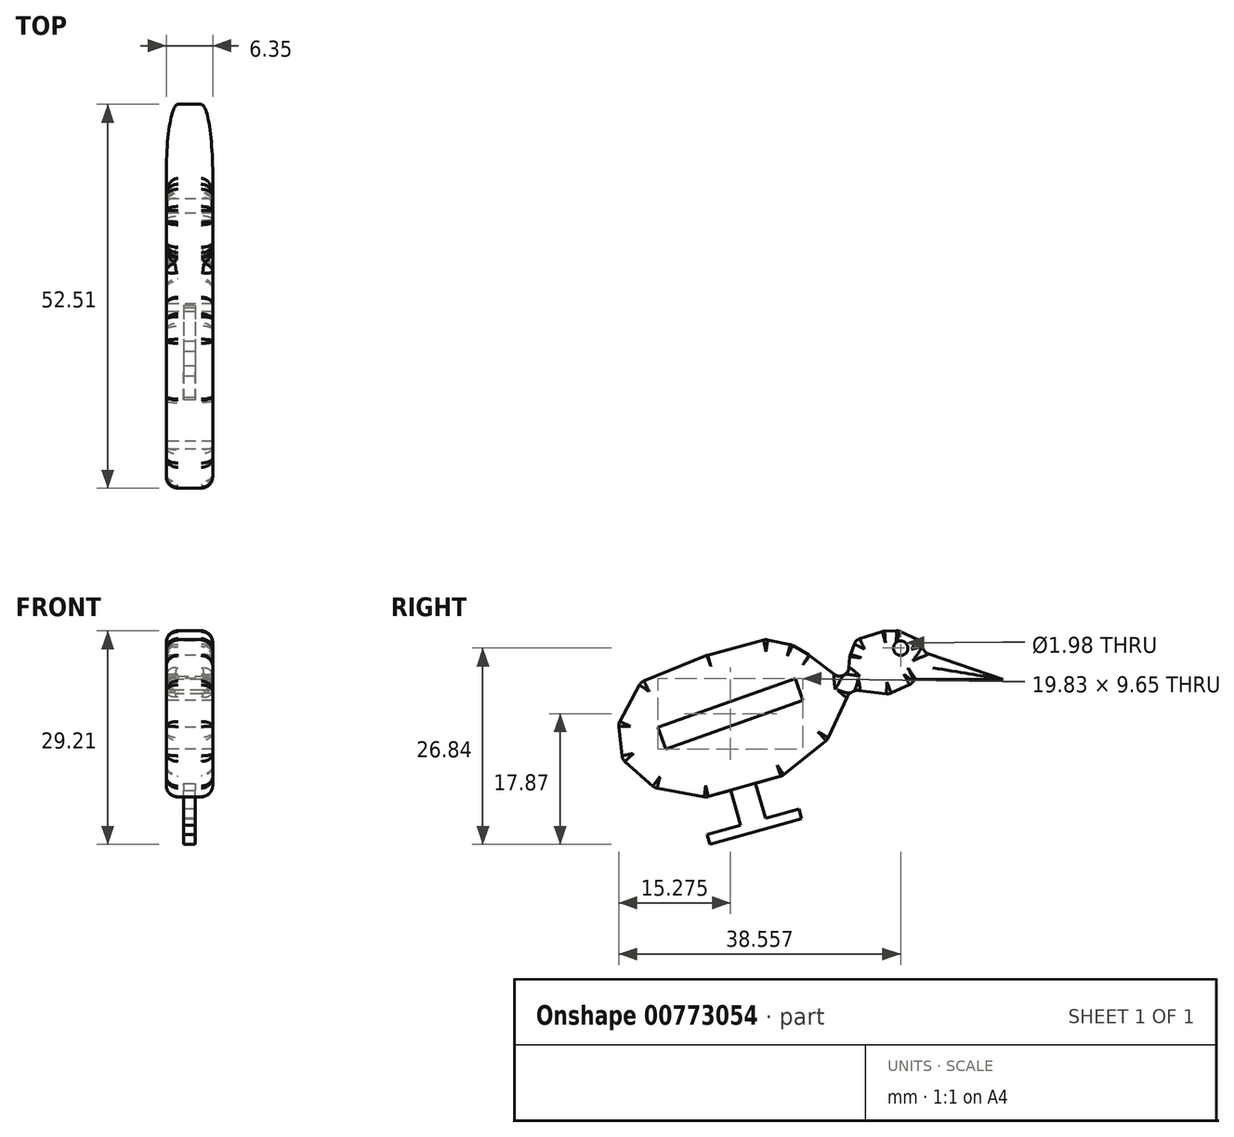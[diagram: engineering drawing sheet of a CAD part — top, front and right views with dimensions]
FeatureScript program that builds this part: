
annotation { "Feature Type Name" : "Feature", "Feature Type Description" : "" }
export const myFeature = defineFeature(function(context is Context, id is Id, definition is map)
    precondition{}
    {
        {
            var Q0;
            Q0=qCreatedBy(makeId("Right.planeOp"),FACE);
            var sketch = newSketch(context, id + "F0", { "sketchPlane" : qUnion([Q0])});
            skLineSegment(sketch, "E0", {"start": v(145.45, 30.35) * mm, "end": v(93.93, 53.96) * mm});
            skLineSegment(sketch, "E1", {"start": v(93.93, 53.96) * mm, "end": v(60.65, 52.9) * mm});
            skLineSegment(sketch, "E2", {"start": v(60.65, 52.9) * mm, "end": v(0, 33.57) * mm});
            skLineSegment(sketch, "E3", {"start": v(-15.57, -37.47) * mm, "end": v(-36.88, -49.23) * mm});
            skLineSegment(sketch, "E4", {"start": v(-469.64, -58.75) * mm, "end": v(-324.72, 0) * mm});
            skLineSegment(sketch, "E5", {"start": v(-469.64, -58.75) * mm, "end": v(-519.02, -150) * mm});
            skLineSegment(sketch, "E6", {"start": v(-519.02, -150) * mm, "end": v(-510.43, -227.28) * mm});
            skLineSegment(sketch, "E7", {"start": v(-510.43, -227.28) * mm, "end": v(-439.58, -289.54) * mm});
            skLineSegment(sketch, "E8", {"start": v(-439.58, -289.54) * mm, "end": v(-326.86, -310.3) * mm});
            skLineSegment(sketch, "E9", {"start": v(-326.86, -310.3) * mm, "end": v(-159.98, -263.53) * mm});
            skLineSegment(sketch, "E10", {"start": v(-159.98, -263.53) * mm, "end": v(-61.37, -183.89) * mm});
            skLineSegment(sketch, "E11", {"start": v(-61.37, -183.89) * mm, "end": v(-15.57, -84.51) * mm});
            skLineSegment(sketch, "E12", {"start": v(-15.57, -84.51) * mm, "end": v(0, -75.92) * mm});
            skLineSegment(sketch, "E13", {"start": v(122.91, -61.97) * mm, "end": v(72.46, -84.51) * mm});
            skLineSegment(sketch, "E14", {"start": v(72.46, -84.51) * mm, "end": v(0, -75.92) * mm});
            skLineSegment(sketch, "E15", {"start": v(122.91, -61.97) * mm, "end": v(150.82, -16.88) * mm});
            skLineSegment(sketch, "E16", {"start": v(150.82, -16.88) * mm, "end": v(145.45, 30.35) * mm});
            skLineSegment(sketch, "E17", {"start": v(0, 33.57) * mm, "end": v(-12.35, 0) * mm});
            skLineSegment(sketch, "E18", {"start": v(-12.35, 0) * mm, "end": v(-15.57, -37.47) * mm});
            skLineSegment(sketch, "E19", {"start": v(-36.88, -49.23) * mm, "end": v(-101.34, 0) * mm});
            skLineSegment(sketch, "E20", {"start": v(-101.34, 0) * mm, "end": v(-140.09, 22.83) * mm});
            skLineSegment(sketch, "E21", {"start": v(-140.09, 22.83) * mm, "end": v(-196.98, 34.64) * mm});
            skLineSegment(sketch, "E22", {"start": v(-196.98, 34.64) * mm, "end": v(-324.72, 0) * mm});
            skLineSegment(sketch, "E23", {"start": v(148.14, 6.73) * mm, "end": v(321.78, -52.74) * mm});
            skLineSegment(sketch, "E24", {"start": v(321.78, -52.74) * mm, "end": v(128.63, -52.74) * mm});
            skSolve(sketch);
        }
        {
            var Q0;
            {var subQ4=sQuery(id+"F0.wireOp",EDGE,"E23");Q0=makeQuery(id+"F0.imprint","IMPRINT",FACE,{"disambiguationData":[TD([[makeQuery(id+"F0.imprint","IMPRINT",EDGE,{"derivedFrom":subQ4}),-1.0]])]});}
            var Q1;
            {var subQ1=sQuery(id+"F0.wireOp",EDGE,"E0");Q1=makeQuery(id+"F0.imprint","IMPRINT",FACE,{"disambiguationData":[TD([[makeQuery(id+"F0.imprint","IMPRINT",EDGE,{"derivedFrom":subQ1}),1.0]])]});}
            extrude(context, id + "F1", {"entities" : qUnion([Q0, Q1]), "depth" : 101.6 * mm, "offsetDistance" : 25.4 * mm});
        }
        {
            var Q0;
            Q0=makeQuery(id+"F1.opExtrude","CAP_EDGE",EDGE,{"disambiguationData":[OSD([sQuery(id+"F0.wireOp",EDGE,"E18")])],"isStart":false});
            var Q1;
            Q1=makeQuery(id+"F1.opExtrude","CAP_EDGE",EDGE,{"disambiguationData":[OSD([sQuery(id+"F0.wireOp",EDGE,"E17")])],"isStart":false});
            var Q2;
            Q2=makeQuery(id+"F1.opExtrude","CAP_EDGE",EDGE,{"disambiguationData":[OSD([sQuery(id+"F0.wireOp",EDGE,"E2")])],"isStart":false});
            var Q3;
            Q3=makeQuery(id+"F1.opExtrude","CAP_EDGE",EDGE,{"disambiguationData":[OSD([sQuery(id+"F0.wireOp",EDGE,"E1")])],"isStart":false});
            var Q4;
            Q4=makeQuery(id+"F1.opExtrude","CAP_EDGE",EDGE,{"disambiguationData":[OSD([sQuery(id+"F0.wireOp",EDGE,"E0")])],"isStart":false});
            var Q5;
            Q5=makeQuery(id+"F1.opExtrude","CAP_EDGE",EDGE,{"disambiguationData":[OSD([sQuery(id+"F0.wireOp",EDGE,"E16")])],"isStart":false});
            var Q6;
            Q6=makeQuery(id+"F1.opExtrude","CAP_EDGE",EDGE,{"disambiguationData":[OSD([sQuery(id+"F0.wireOp",EDGE,"E23")])],"isStart":false});
            var Q7;
            Q7=makeQuery(id+"F1.opExtrude","CAP_EDGE",EDGE,{"disambiguationData":[OSD([sQuery(id+"F0.wireOp",EDGE,"E14")])],"isStart":false});
            var Q8;
            Q8=makeQuery(id+"F1.opExtrude","CAP_EDGE",EDGE,{"disambiguationData":[OSD([sQuery(id+"F0.wireOp",EDGE,"E13")])],"isStart":false});
            var Q9;
            Q9=makeQuery(id+"F1.opExtrude","CAP_EDGE",EDGE,{"disambiguationData":[OSD([sQuery(id+"F0.wireOp",EDGE,"E15")])],"isStart":false});
            var Q10;
            Q10=makeQuery(id+"F1.opExtrude","CAP_EDGE",EDGE,{"disambiguationData":[OSD([sQuery(id+"F0.wireOp",EDGE,"E24")])],"isStart":false});
            fillet(context, id + "F2", {"entities" : qUnion([Q0, Q1, Q2, Q3, Q4, Q5, Q6, Q7, Q8, Q9, Q10]), "radius" : 25.4 * mm, "tangentPropagation" : true, "allowEdgeOverflow" : false});
        }
        {
            var Q0;
            Q0=makeQuery(id+"F1.opExtrude","CAP_EDGE",EDGE,{"disambiguationData":[OSD([sQuery(id+"F0.wireOp",EDGE,"E23")])],"isStart":true});
            var Q1;
            Q1=makeQuery(id+"F1.opExtrude","CAP_EDGE",EDGE,{"disambiguationData":[OSD([sQuery(id+"F0.wireOp",EDGE,"E16")])],"isStart":true});
            var Q2;
            Q2=makeQuery(id+"F1.opExtrude","CAP_EDGE",EDGE,{"disambiguationData":[OSD([sQuery(id+"F0.wireOp",EDGE,"E1")])],"isStart":true});
            var Q3;
            Q3=makeQuery(id+"F1.opExtrude","CAP_EDGE",EDGE,{"disambiguationData":[OSD([sQuery(id+"F0.wireOp",EDGE,"E0")])],"isStart":true});
            var Q4;
            Q4=makeQuery(id+"F1.opExtrude","CAP_EDGE",EDGE,{"disambiguationData":[OSD([sQuery(id+"F0.wireOp",EDGE,"E2")])],"isStart":true});
            var Q5;
            Q5=makeQuery(id+"F1.opExtrude","CAP_EDGE",EDGE,{"disambiguationData":[OSD([sQuery(id+"F0.wireOp",EDGE,"E17")])],"isStart":true});
            var Q6;
            Q6=makeQuery(id+"F1.opExtrude","CAP_EDGE",EDGE,{"disambiguationData":[OSD([sQuery(id+"F0.wireOp",EDGE,"E18")])],"isStart":true});
            var Q7;
            Q7=makeQuery(id+"F1.opExtrude","CAP_EDGE",EDGE,{"disambiguationData":[OSD([sQuery(id+"F0.wireOp",EDGE,"E14")])],"isStart":true});
            var Q8;
            Q8=makeQuery(id+"F1.opExtrude","CAP_EDGE",EDGE,{"disambiguationData":[OSD([sQuery(id+"F0.wireOp",EDGE,"E13")])],"isStart":true});
            var Q9;
            Q9=makeQuery(id+"F1.opExtrude","CAP_EDGE",EDGE,{"disambiguationData":[OSD([sQuery(id+"F0.wireOp",EDGE,"E15")])],"isStart":true});
            var Q10;
            Q10=makeQuery(id+"F1.opExtrude","CAP_EDGE",EDGE,{"disambiguationData":[OSD([sQuery(id+"F0.wireOp",EDGE,"E24")])],"isStart":true});
            fillet(context, id + "F3", {"entities" : qUnion([Q0, Q1, Q2, Q3, Q4, Q5, Q6, Q7, Q8, Q9, Q10]), "radius" : 25.4 * mm, "tangentPropagation" : true, "allowEdgeOverflow" : false});
        }
        {
            var Q0;
            Q0=makeQuery(id+"F1.opExtrude","CAP_EDGE",EDGE,{"disambiguationData":[OSD([sQuery(id+"F0.wireOp",EDGE,"E3")])],"isStart":true});
            var Q1;
            Q1=makeQuery(id+"F1.opExtrude","CAP_EDGE",EDGE,{"disambiguationData":[OSD([sQuery(id+"F0.wireOp",EDGE,"E12")])],"isStart":true});
            var Q2;
            Q2=makeQuery(id+"F1.opExtrude","CAP_EDGE",EDGE,{"disambiguationData":[OSD([sQuery(id+"F0.wireOp",EDGE,"E3")])],"isStart":false});
            var Q3;
            Q3=makeQuery(id+"F1.opExtrude","CAP_EDGE",EDGE,{"disambiguationData":[OSD([sQuery(id+"F0.wireOp",EDGE,"E12")])],"isStart":false});
            fillet(context, id + "F4", {"entities" : qUnion([Q0, Q1, Q2, Q3]), "radius" : 19.05 * mm, "tangentPropagation" : true, "allowEdgeOverflow" : false});
        }
        {
            var Q0;
            Q0=makeQuery(id+"F1.opExtrude","CAP_EDGE",EDGE,{"disambiguationData":[OSD([sQuery(id+"F0.wireOp",EDGE,"E19")])],"isStart":true});
            var Q1;
            Q1=makeQuery(id+"F1.opExtrude","CAP_EDGE",EDGE,{"disambiguationData":[OSD([sQuery(id+"F0.wireOp",EDGE,"E11")])],"isStart":true});
            var Q2;
            Q2=makeQuery(id+"F1.opExtrude","CAP_EDGE",EDGE,{"disambiguationData":[OSD([sQuery(id+"F0.wireOp",EDGE,"E10")])],"isStart":true});
            var Q3;
            Q3=makeQuery(id+"F1.opExtrude","CAP_EDGE",EDGE,{"disambiguationData":[OSD([sQuery(id+"F0.wireOp",EDGE,"E9")])],"isStart":true});
            var Q4;
            Q4=makeQuery(id+"F1.opExtrude","CAP_EDGE",EDGE,{"disambiguationData":[OSD([sQuery(id+"F0.wireOp",EDGE,"E8")])],"isStart":true});
            var Q5;
            Q5=makeQuery(id+"F1.opExtrude","CAP_EDGE",EDGE,{"disambiguationData":[OSD([sQuery(id+"F0.wireOp",EDGE,"E7")])],"isStart":true});
            var Q6;
            Q6=makeQuery(id+"F1.opExtrude","CAP_EDGE",EDGE,{"disambiguationData":[OSD([sQuery(id+"F0.wireOp",EDGE,"E6")])],"isStart":true});
            var Q7;
            Q7=makeQuery(id+"F1.opExtrude","CAP_EDGE",EDGE,{"disambiguationData":[OSD([sQuery(id+"F0.wireOp",EDGE,"E5")])],"isStart":true});
            var Q8;
            Q8=makeQuery(id+"F1.opExtrude","CAP_EDGE",EDGE,{"disambiguationData":[OSD([sQuery(id+"F0.wireOp",EDGE,"E4")])],"isStart":true});
            var Q9;
            Q9=makeQuery(id+"F1.opExtrude","CAP_EDGE",EDGE,{"disambiguationData":[OSD([sQuery(id+"F0.wireOp",EDGE,"E22")])],"isStart":true});
            var Q10;
            Q10=makeQuery(id+"F1.opExtrude","CAP_EDGE",EDGE,{"disambiguationData":[OSD([sQuery(id+"F0.wireOp",EDGE,"E21")])],"isStart":true});
            var Q11;
            Q11=makeQuery(id+"F1.opExtrude","CAP_EDGE",EDGE,{"disambiguationData":[OSD([sQuery(id+"F0.wireOp",EDGE,"E20")])],"isStart":true});
            var Q12;
            Q12=makeQuery(id+"F1.opExtrude","CAP_EDGE",EDGE,{"disambiguationData":[OSD([sQuery(id+"F0.wireOp",EDGE,"E6")])],"isStart":false});
            var Q13;
            Q13=makeQuery(id+"F1.opExtrude","CAP_EDGE",EDGE,{"disambiguationData":[OSD([sQuery(id+"F0.wireOp",EDGE,"E5")])],"isStart":false});
            var Q14;
            Q14=makeQuery(id+"F1.opExtrude","CAP_EDGE",EDGE,{"disambiguationData":[OSD([sQuery(id+"F0.wireOp",EDGE,"E7")])],"isStart":false});
            var Q15;
            Q15=makeQuery(id+"F1.opExtrude","CAP_EDGE",EDGE,{"disambiguationData":[OSD([sQuery(id+"F0.wireOp",EDGE,"E8")])],"isStart":false});
            var Q16;
            Q16=makeQuery(id+"F1.opExtrude","CAP_EDGE",EDGE,{"disambiguationData":[OSD([sQuery(id+"F0.wireOp",EDGE,"E9")])],"isStart":false});
            var Q17;
            Q17=makeQuery(id+"F1.opExtrude","CAP_EDGE",EDGE,{"disambiguationData":[OSD([sQuery(id+"F0.wireOp",EDGE,"E10")])],"isStart":false});
            var Q18;
            Q18=makeQuery(id+"F1.opExtrude","CAP_EDGE",EDGE,{"disambiguationData":[OSD([sQuery(id+"F0.wireOp",EDGE,"E11")])],"isStart":false});
            var Q19;
            Q19=makeQuery(id+"F1.opExtrude","CAP_EDGE",EDGE,{"disambiguationData":[OSD([sQuery(id+"F0.wireOp",EDGE,"E19")])],"isStart":false});
            var Q20;
            Q20=makeQuery(id+"F1.opExtrude","CAP_EDGE",EDGE,{"disambiguationData":[OSD([sQuery(id+"F0.wireOp",EDGE,"E20")])],"isStart":false});
            var Q21;
            Q21=makeQuery(id+"F1.opExtrude","CAP_EDGE",EDGE,{"disambiguationData":[OSD([sQuery(id+"F0.wireOp",EDGE,"E21")])],"isStart":false});
            var Q22;
            Q22=makeQuery(id+"F1.opExtrude","CAP_EDGE",EDGE,{"disambiguationData":[OSD([sQuery(id+"F0.wireOp",EDGE,"E4")])],"isStart":false});
            var Q23;
            Q23=makeQuery(id+"F1.opExtrude","CAP_EDGE",EDGE,{"disambiguationData":[OSD([sQuery(id+"F0.wireOp",EDGE,"E22")])],"isStart":false});
            fillet(context, id + "F5", {"entities" : qUnion([Q0, Q1, Q2, Q3, Q4, Q5, Q6, Q7, Q8, Q9, Q10, Q11, Q12, Q13, Q14, Q15, Q16, Q17, Q18, Q19, Q20, Q21, Q22, Q23]), "radius" : 25.4 * mm, "tangentPropagation" : true, "allowEdgeOverflow" : false});
        }
        {
            var Q0;
            Q0=makeQuery(id+"F1.opExtrude","SWEPT_EDGE",EDGE,{"disambiguationData":[OSD([sQuery(id+"F0.wireOp",EDGE,"E15"),sQuery(id+"F0.wireOp",EDGE,"E24")])]});
            fillet(context, id + "F6", {"entities" : qUnion([Q0]), "radius" : 5.08 * mm, "tangentPropagation" : true, "allowEdgeOverflow" : false});
        }
        {
            var Q0;
            Q0=makeQuery(id+"F1.opExtrude","SWEPT_EDGE",EDGE,{"disambiguationData":[OSD([sQuery(id+"F0.wireOp",EDGE,"E13"),sQuery(id+"F0.wireOp",EDGE,"E15")])]});
            var Q1;
            Q1=makeQuery(id+"F1.opExtrude","SWEPT_EDGE",EDGE,{"disambiguationData":[OSD([sQuery(id+"F0.wireOp",EDGE,"E13"),sQuery(id+"F0.wireOp",EDGE,"E14")])]});
            var Q2;
            Q2=makeQuery(id+"F1.opExtrude","SWEPT_EDGE",EDGE,{"disambiguationData":[OSD([sQuery(id+"F0.wireOp",EDGE,"E12"),sQuery(id+"F0.wireOp",EDGE,"E14")])]});
            var Q3;
            Q3=makeQuery(id+"F1.opExtrude","SWEPT_EDGE",EDGE,{"disambiguationData":[OSD([sQuery(id+"F0.wireOp",EDGE,"E11"),sQuery(id+"F0.wireOp",EDGE,"E12")])]});
            var Q4;
            Q4=makeQuery(id+"F1.opExtrude","SWEPT_EDGE",EDGE,{"disambiguationData":[OSD([sQuery(id+"F0.wireOp",EDGE,"E10"),sQuery(id+"F0.wireOp",EDGE,"E11")])]});
            var Q5;
            Q5=makeQuery(id+"F1.opExtrude","SWEPT_EDGE",EDGE,{"disambiguationData":[OSD([sQuery(id+"F0.wireOp",EDGE,"E9"),sQuery(id+"F0.wireOp",EDGE,"E10")])]});
            var Q6;
            Q6=makeQuery(id+"F1.opExtrude","SWEPT_EDGE",EDGE,{"disambiguationData":[OSD([sQuery(id+"F0.wireOp",EDGE,"E8"),sQuery(id+"F0.wireOp",EDGE,"E9")])]});
            var Q7;
            Q7=makeQuery(id+"F1.opExtrude","SWEPT_EDGE",EDGE,{"disambiguationData":[OSD([sQuery(id+"F0.wireOp",EDGE,"E7"),sQuery(id+"F0.wireOp",EDGE,"E8")])]});
            var Q8;
            Q8=makeQuery(id+"F1.opExtrude","SWEPT_EDGE",EDGE,{"disambiguationData":[OSD([sQuery(id+"F0.wireOp",EDGE,"E6"),sQuery(id+"F0.wireOp",EDGE,"E7")])]});
            var Q9;
            Q9=makeQuery(id+"F1.opExtrude","SWEPT_EDGE",EDGE,{"disambiguationData":[OSD([sQuery(id+"F0.wireOp",EDGE,"E5"),sQuery(id+"F0.wireOp",EDGE,"E6")])]});
            var Q10;
            Q10=makeQuery(id+"F1.opExtrude","SWEPT_EDGE",EDGE,{"disambiguationData":[OSD([sQuery(id+"F0.wireOp",EDGE,"E4"),sQuery(id+"F0.wireOp",EDGE,"E5")])]});
            var Q11;
            Q11=makeQuery(id+"F1.opExtrude","SWEPT_EDGE",EDGE,{"disambiguationData":[OSD([sQuery(id+"F0.wireOp",EDGE,"E4"),sQuery(id+"F0.wireOp",EDGE,"E22")])]});
            var Q12;
            Q12=makeQuery(id+"F1.opExtrude","SWEPT_EDGE",EDGE,{"disambiguationData":[OSD([sQuery(id+"F0.wireOp",EDGE,"E21"),sQuery(id+"F0.wireOp",EDGE,"E22")])]});
            var Q13;
            Q13=makeQuery(id+"F1.opExtrude","SWEPT_EDGE",EDGE,{"disambiguationData":[OSD([sQuery(id+"F0.wireOp",EDGE,"E20"),sQuery(id+"F0.wireOp",EDGE,"E21")])]});
            var Q14;
            Q14=makeQuery(id+"F1.opExtrude","SWEPT_EDGE",EDGE,{"disambiguationData":[OSD([sQuery(id+"F0.wireOp",EDGE,"E19"),sQuery(id+"F0.wireOp",EDGE,"E20")])]});
            var Q15;
            Q15=makeQuery(id+"F1.opExtrude","SWEPT_EDGE",EDGE,{"disambiguationData":[OSD([sQuery(id+"F0.wireOp",EDGE,"E3"),sQuery(id+"F0.wireOp",EDGE,"E19")])]});
            var Q16;
            Q16=makeQuery(id+"F1.opExtrude","SWEPT_EDGE",EDGE,{"disambiguationData":[OSD([sQuery(id+"F0.wireOp",EDGE,"E3"),sQuery(id+"F0.wireOp",EDGE,"E18")])]});
            var Q17;
            Q17=makeQuery(id+"F1.opExtrude","SWEPT_EDGE",EDGE,{"disambiguationData":[OSD([sQuery(id+"F0.wireOp",EDGE,"E17"),sQuery(id+"F0.wireOp",EDGE,"E18")])]});
            var Q18;
            Q18=makeQuery(id+"F1.opExtrude","SWEPT_EDGE",EDGE,{"disambiguationData":[OSD([sQuery(id+"F0.wireOp",EDGE,"E2"),sQuery(id+"F0.wireOp",EDGE,"E17")])]});
            var Q19;
            Q19=makeQuery(id+"F1.opExtrude","SWEPT_EDGE",EDGE,{"disambiguationData":[OSD([sQuery(id+"F0.wireOp",EDGE,"E1"),sQuery(id+"F0.wireOp",EDGE,"E2")])]});
            var Q20;
            Q20=makeQuery(id+"F1.opExtrude","SWEPT_EDGE",EDGE,{"disambiguationData":[OSD([sQuery(id+"F0.wireOp",EDGE,"E0"),sQuery(id+"F0.wireOp",EDGE,"E1")])]});
            var Q21;
            Q21=makeQuery(id+"F1.opExtrude","SWEPT_EDGE",EDGE,{"disambiguationData":[OSD([sQuery(id+"F0.wireOp",EDGE,"E0"),sQuery(id+"F0.wireOp",EDGE,"E16")])]});
            var Q22;
            Q22=makeQuery(id+"F1.opExtrude","SWEPT_EDGE",EDGE,{"disambiguationData":[OSD([sQuery(id+"F0.wireOp",EDGE,"E16"),sQuery(id+"F0.wireOp",EDGE,"E23")])]});
            fillet(context, id + "F7", {"entities" : qUnion([Q0, Q1, Q2, Q3, Q4, Q5, Q6, Q7, Q8, Q9, Q10, Q11, Q12, Q13, Q14, Q15, Q16, Q17, Q18, Q19, Q20, Q21, Q22]), "radius" : 19.05 * mm, "tangentPropagation" : true, "allowEdgeOverflow" : false});
        }
        {
            var Q0;
            Q0=makeQuery(id+"F1.opExtrude","CAP_FACE",FACE,{"disambiguationData":[OSD([sQuery(id+"F0.wireOp",EDGE,"E0"),sQuery(id+"F0.wireOp",EDGE,"E1"),sQuery(id+"F0.wireOp",EDGE,"E2"),sQuery(id+"F0.wireOp",EDGE,"E3"),sQuery(id+"F0.wireOp",EDGE,"E4"),sQuery(id+"F0.wireOp",EDGE,"E5"),sQuery(id+"F0.wireOp",EDGE,"E6"),sQuery(id+"F0.wireOp",EDGE,"E7"),sQuery(id+"F0.wireOp",EDGE,"E8"),sQuery(id+"F0.wireOp",EDGE,"E9"),sQuery(id+"F0.wireOp",EDGE,"E10"),sQuery(id+"F0.wireOp",EDGE,"E11"),sQuery(id+"F0.wireOp",EDGE,"E12"),sQuery(id+"F0.wireOp",EDGE,"E13"),sQuery(id+"F0.wireOp",EDGE,"E14"),sQuery(id+"F0.wireOp",EDGE,"E15"),sQuery(id+"F0.wireOp",EDGE,"E16"),sQuery(id+"F0.wireOp",EDGE,"E17"),sQuery(id+"F0.wireOp",EDGE,"E18"),sQuery(id+"F0.wireOp",EDGE,"E19"),sQuery(id+"F0.wireOp",EDGE,"E20"),sQuery(id+"F0.wireOp",EDGE,"E21"),sQuery(id+"F0.wireOp",EDGE,"E22"),sQuery(id+"F0.wireOp",EDGE,"E23"),sQuery(id+"F0.wireOp",EDGE,"E24")])],"isStart":true});
            var sketch = newSketch(context, id + "F8", { "sketchPlane" : qUnion([Q0])});
            skCircle(sketch, "E25", {"center": v(-98.51, 15.85) * mm, "radius": 15.88 * mm});
            skSolve(sketch);
        }
        {
            var Q0;
            {var subQ0=sQuery(id+"F8.wireOp",EDGE,"E25");var subQ1=sQuery(id+"F0.wireOp",EDGE,"E0");var subQ2=makeQuery(id+"F3.opFillet","BLEND_EDGE",EDGE,{"blendedFrom":[makeQuery(id+"F1.opExtrude","CAP_EDGE",EDGE,{"disambiguationData":[OSD([subQ1])],"isStart":true}),makeQuery(id+"F1.opExtrude","CAP_FACE",FACE,{"disambiguationData":[OSD([subQ1,sQuery(id+"F0.wireOp",EDGE,"E1"),sQuery(id+"F0.wireOp",EDGE,"E2"),sQuery(id+"F0.wireOp",EDGE,"E3"),sQuery(id+"F0.wireOp",EDGE,"E4"),sQuery(id+"F0.wireOp",EDGE,"E5"),sQuery(id+"F0.wireOp",EDGE,"E6"),sQuery(id+"F0.wireOp",EDGE,"E7"),sQuery(id+"F0.wireOp",EDGE,"E8"),sQuery(id+"F0.wireOp",EDGE,"E9"),sQuery(id+"F0.wireOp",EDGE,"E10"),sQuery(id+"F0.wireOp",EDGE,"E11"),sQuery(id+"F0.wireOp",EDGE,"E12"),sQuery(id+"F0.wireOp",EDGE,"E13"),sQuery(id+"F0.wireOp",EDGE,"E14"),sQuery(id+"F0.wireOp",EDGE,"E15"),sQuery(id+"F0.wireOp",EDGE,"E16"),sQuery(id+"F0.wireOp",EDGE,"E17"),sQuery(id+"F0.wireOp",EDGE,"E18"),sQuery(id+"F0.wireOp",EDGE,"E19"),sQuery(id+"F0.wireOp",EDGE,"E20"),sQuery(id+"F0.wireOp",EDGE,"E21"),sQuery(id+"F0.wireOp",EDGE,"E22"),sQuery(id+"F0.wireOp",EDGE,"E23"),sQuery(id+"F0.wireOp",EDGE,"E24")])],"isStart":true})],"blendedInto":[makeQuery(id+"F1.opExtrude","CAP_FACE",FACE,{"disambiguationData":[OSD([subQ1,sQuery(id+"F0.wireOp",EDGE,"E1"),sQuery(id+"F0.wireOp",EDGE,"E2"),sQuery(id+"F0.wireOp",EDGE,"E3"),sQuery(id+"F0.wireOp",EDGE,"E4"),sQuery(id+"F0.wireOp",EDGE,"E5"),sQuery(id+"F0.wireOp",EDGE,"E6"),sQuery(id+"F0.wireOp",EDGE,"E7"),sQuery(id+"F0.wireOp",EDGE,"E8"),sQuery(id+"F0.wireOp",EDGE,"E9"),sQuery(id+"F0.wireOp",EDGE,"E10"),sQuery(id+"F0.wireOp",EDGE,"E11"),sQuery(id+"F0.wireOp",EDGE,"E12"),sQuery(id+"F0.wireOp",EDGE,"E13"),sQuery(id+"F0.wireOp",EDGE,"E14"),sQuery(id+"F0.wireOp",EDGE,"E15"),sQuery(id+"F0.wireOp",EDGE,"E16"),sQuery(id+"F0.wireOp",EDGE,"E17"),sQuery(id+"F0.wireOp",EDGE,"E18"),sQuery(id+"F0.wireOp",EDGE,"E19"),sQuery(id+"F0.wireOp",EDGE,"E20"),sQuery(id+"F0.wireOp",EDGE,"E21"),sQuery(id+"F0.wireOp",EDGE,"E22"),sQuery(id+"F0.wireOp",EDGE,"E23"),sQuery(id+"F0.wireOp",EDGE,"E24")])],"isStart":true})]});var subQ3=makeQuery(id+"F8.imprint","INTERSECT",VERTEX,{"disambiguationData":[OD(0.0)],"derivedFrom":[subQ2,subQ0]});Q0=makeQuery(id+"F8.imprint","IMPRINT",FACE,{"disambiguationData":[TD([[makeQuery(id+"F8.imprint","IMPRINT",EDGE,{"disambiguationData":[TD([[subQ3,1.0]])],"derivedFrom":subQ0}),1.0]])]});}
            var Q1;
            {var subQ0=sQuery(id+"F8.wireOp",EDGE,"E25");var subQ1=sQuery(id+"F0.wireOp",EDGE,"E0");var subQ2=makeQuery(id+"F3.opFillet","BLEND_EDGE",EDGE,{"blendedFrom":[makeQuery(id+"F1.opExtrude","CAP_EDGE",EDGE,{"disambiguationData":[OSD([subQ1])],"isStart":true}),makeQuery(id+"F1.opExtrude","CAP_FACE",FACE,{"disambiguationData":[OSD([subQ1,sQuery(id+"F0.wireOp",EDGE,"E1"),sQuery(id+"F0.wireOp",EDGE,"E2"),sQuery(id+"F0.wireOp",EDGE,"E3"),sQuery(id+"F0.wireOp",EDGE,"E4"),sQuery(id+"F0.wireOp",EDGE,"E5"),sQuery(id+"F0.wireOp",EDGE,"E6"),sQuery(id+"F0.wireOp",EDGE,"E7"),sQuery(id+"F0.wireOp",EDGE,"E8"),sQuery(id+"F0.wireOp",EDGE,"E9"),sQuery(id+"F0.wireOp",EDGE,"E10"),sQuery(id+"F0.wireOp",EDGE,"E11"),sQuery(id+"F0.wireOp",EDGE,"E12"),sQuery(id+"F0.wireOp",EDGE,"E13"),sQuery(id+"F0.wireOp",EDGE,"E14"),sQuery(id+"F0.wireOp",EDGE,"E15"),sQuery(id+"F0.wireOp",EDGE,"E16"),sQuery(id+"F0.wireOp",EDGE,"E17"),sQuery(id+"F0.wireOp",EDGE,"E18"),sQuery(id+"F0.wireOp",EDGE,"E19"),sQuery(id+"F0.wireOp",EDGE,"E20"),sQuery(id+"F0.wireOp",EDGE,"E21"),sQuery(id+"F0.wireOp",EDGE,"E22"),sQuery(id+"F0.wireOp",EDGE,"E23"),sQuery(id+"F0.wireOp",EDGE,"E24")])],"isStart":true})],"blendedInto":[makeQuery(id+"F1.opExtrude","CAP_FACE",FACE,{"disambiguationData":[OSD([subQ1,sQuery(id+"F0.wireOp",EDGE,"E1"),sQuery(id+"F0.wireOp",EDGE,"E2"),sQuery(id+"F0.wireOp",EDGE,"E3"),sQuery(id+"F0.wireOp",EDGE,"E4"),sQuery(id+"F0.wireOp",EDGE,"E5"),sQuery(id+"F0.wireOp",EDGE,"E6"),sQuery(id+"F0.wireOp",EDGE,"E7"),sQuery(id+"F0.wireOp",EDGE,"E8"),sQuery(id+"F0.wireOp",EDGE,"E9"),sQuery(id+"F0.wireOp",EDGE,"E10"),sQuery(id+"F0.wireOp",EDGE,"E11"),sQuery(id+"F0.wireOp",EDGE,"E12"),sQuery(id+"F0.wireOp",EDGE,"E13"),sQuery(id+"F0.wireOp",EDGE,"E14"),sQuery(id+"F0.wireOp",EDGE,"E15"),sQuery(id+"F0.wireOp",EDGE,"E16"),sQuery(id+"F0.wireOp",EDGE,"E17"),sQuery(id+"F0.wireOp",EDGE,"E18"),sQuery(id+"F0.wireOp",EDGE,"E19"),sQuery(id+"F0.wireOp",EDGE,"E20"),sQuery(id+"F0.wireOp",EDGE,"E21"),sQuery(id+"F0.wireOp",EDGE,"E22"),sQuery(id+"F0.wireOp",EDGE,"E23"),sQuery(id+"F0.wireOp",EDGE,"E24")])],"isStart":true})]});var subQ3=makeQuery(id+"F8.imprint","INTERSECT",VERTEX,{"disambiguationData":[OD(0.0)],"derivedFrom":[subQ2,subQ0]});Q1=makeQuery(id+"F8.imprint","IMPRINT",FACE,{"disambiguationData":[TD([[makeQuery(id+"F8.imprint","IMPRINT",EDGE,{"disambiguationData":[TD([[subQ3,-1.0]])],"derivedFrom":subQ0}),1.0]])]});}
            extrude(context, id + "F9", {"entities" : qUnion([Q0, Q1]), "operationType" : NewBodyOperationType.REMOVE, "oppositeDirection" : true, "depth" : 101.6 * mm, "offsetDistance" : 25.4 * mm});
        }
        {
            var Q0;
            Q0=makeQuery(id+"F1.opExtrude","CAP_FACE",FACE,{"disambiguationData":[OSD([sQuery(id+"F0.wireOp",EDGE,"E0"),sQuery(id+"F0.wireOp",EDGE,"E1"),sQuery(id+"F0.wireOp",EDGE,"E2"),sQuery(id+"F0.wireOp",EDGE,"E3"),sQuery(id+"F0.wireOp",EDGE,"E4"),sQuery(id+"F0.wireOp",EDGE,"E5"),sQuery(id+"F0.wireOp",EDGE,"E6"),sQuery(id+"F0.wireOp",EDGE,"E7"),sQuery(id+"F0.wireOp",EDGE,"E8"),sQuery(id+"F0.wireOp",EDGE,"E9"),sQuery(id+"F0.wireOp",EDGE,"E10"),sQuery(id+"F0.wireOp",EDGE,"E11"),sQuery(id+"F0.wireOp",EDGE,"E12"),sQuery(id+"F0.wireOp",EDGE,"E13"),sQuery(id+"F0.wireOp",EDGE,"E14"),sQuery(id+"F0.wireOp",EDGE,"E15"),sQuery(id+"F0.wireOp",EDGE,"E16"),sQuery(id+"F0.wireOp",EDGE,"E17"),sQuery(id+"F0.wireOp",EDGE,"E18"),sQuery(id+"F0.wireOp",EDGE,"E19"),sQuery(id+"F0.wireOp",EDGE,"E20"),sQuery(id+"F0.wireOp",EDGE,"E21"),sQuery(id+"F0.wireOp",EDGE,"E22"),sQuery(id+"F0.wireOp",EDGE,"E23"),sQuery(id+"F0.wireOp",EDGE,"E24")])],"isStart":true});
            var sketch = newSketch(context, id + "F10", { "sketchPlane" : qUnion([Q0])});
            skLineSegment(sketch, "E26", {"start": v(132.35, -50.45) * mm, "end": v(115.36, -98.32) * mm});
            skLineSegment(sketch, "E27", {"start": v(115.36, -98.32) * mm, "end": v(415.64, -204.9) * mm});
            skLineSegment(sketch, "E28", {"start": v(415.64, -204.9) * mm, "end": v(432.63, -157.02) * mm});
            skLineSegment(sketch, "E29", {"start": v(432.63, -157.02) * mm, "end": v(132.35, -50.45) * mm});
            skSolve(sketch);
        }
        {
            var Q0;
            Q0=makeQuery(id+"F10.imprint","IMPRINT",FACE,{"disambiguationData":[TD([[makeQuery(id+"F10.imprint","IMPRINT",EDGE,{"derivedFrom":sQuery(id+"F10.wireOp",EDGE,"E26")}),1.0]])]});
            extrude(context, id + "F11", {"entities" : qUnion([Q0]), "operationType" : NewBodyOperationType.REMOVE, "oppositeDirection" : true, "depth" : 101.6 * mm, "offsetDistance" : 25.4 * mm});
        }
        {
            var Q0;
            Q0=makeQuery(id+"F1.opExtrude","SWEPT_FACE",FACE,{"disambiguationData":[OSD([sQuery(id+"F0.wireOp",EDGE,"E9")])]});
            var sketch = newSketch(context, id + "F12", { "sketchPlane" : qUnion([Q0])});
            skLineSegment(sketch, "E30.bottom", {"start": v(37.89, 286.5) * mm, "end": v(63.29, 286.5) * mm});
            skLineSegment(sketch, "E30.top", {"start": v(37.89, 342.37) * mm, "end": v(63.29, 342.37) * mm});
            skLineSegment(sketch, "E30.left", {"start": v(37.89, 286.5) * mm, "end": v(37.89, 342.37) * mm});
            skLineSegment(sketch, "E30.right", {"start": v(63.29, 286.5) * mm, "end": v(63.29, 342.37) * mm});
            skSolve(sketch);
        }
        {
            var Q0;
            Q0=makeQuery(id+"F12.imprint","IMPRINT",FACE,{"disambiguationData":[TD([[makeQuery(id+"F12.imprint","IMPRINT",EDGE,{"derivedFrom":sQuery(id+"F12.wireOp",EDGE,"E30.bottom")}),1.0]])]});
            extrude(context, id + "F13", {"entities" : qUnion([Q0]), "operationType" : NewBodyOperationType.ADD, "depth" : 101.6 * mm, "offsetDistance" : 25.4 * mm});
        }
        {
            var Q0;
            Q0=makeQuery(id+"F13.opExtrude","SWEPT_FACE",FACE,{"disambiguationData":[OSD([sQuery(id+"F12.wireOp",EDGE,"E30.bottom")])]});
            var sketch = newSketch(context, id + "F14", { "sketchPlane" : qUnion([Q0])});
            skLineSegment(sketch, "E31.bottom", {"start": v(-63.29, -312.17) * mm, "end": v(-37.89, -312.17) * mm});
            skLineSegment(sketch, "E31.top", {"start": v(-63.29, -290.47) * mm, "end": v(-37.89, -290.47) * mm});
            skLineSegment(sketch, "E31.left", {"start": v(-63.29, -312.17) * mm, "end": v(-63.29, -290.47) * mm});
            skLineSegment(sketch, "E31.right", {"start": v(-37.89, -312.17) * mm, "end": v(-37.89, -290.47) * mm});
            skSolve(sketch);
        }
        {
            var Q0;
            Q0=makeQuery(id+"F14.imprint","IMPRINT",FACE,{"disambiguationData":[TD([[makeQuery(id+"F14.imprint","IMPRINT",EDGE,{"derivedFrom":sQuery(id+"F14.wireOp",EDGE,"E31.bottom")}),-1.0]])]});
            extrude(context, id + "F15", {"entities" : qUnion([Q0]), "operationType" : NewBodyOperationType.ADD, "depth" : 76.2 * mm, "offsetDistance" : 25.4 * mm});
        }
        {
            var Q0;
            Q0=makeQuery(id+"F13.opExtrude","SWEPT_FACE",FACE,{"disambiguationData":[OSD([sQuery(id+"F12.wireOp",EDGE,"E30.top")])]});
            var sketch = newSketch(context, id + "F16", { "sketchPlane" : qUnion([Q0])});
            skLineSegment(sketch, "E32.bottom", {"start": v(63.29, -312.17) * mm, "end": v(37.89, -312.17) * mm});
            skLineSegment(sketch, "E32.top", {"start": v(63.29, -289.7) * mm, "end": v(37.89, -289.7) * mm});
            skLineSegment(sketch, "E32.left", {"start": v(63.29, -312.17) * mm, "end": v(63.29, -289.7) * mm});
            skLineSegment(sketch, "E32.right", {"start": v(37.89, -312.17) * mm, "end": v(37.89, -289.7) * mm});
            skSolve(sketch);
        }
        {
            var Q0;
            Q0=makeQuery(id+"F16.imprint","IMPRINT",FACE,{"disambiguationData":[TD([[makeQuery(id+"F16.imprint","IMPRINT",EDGE,{"derivedFrom":sQuery(id+"F16.wireOp",EDGE,"E32.bottom")}),1.0]])]});
            extrude(context, id + "F17", {"entities" : qUnion([Q0]), "operationType" : NewBodyOperationType.ADD, "depth" : 76.2 * mm, "offsetDistance" : 25.4 * mm});
        }
        {
            var Q0;
            Q0=makeQuery(id+"F1.opExtrude","SWEPT_BODY",BODY,{"disambiguationData":[OSD([sQuery(id+"F0.wireOp",EDGE,"E0"),sQuery(id+"F0.wireOp",EDGE,"E1"),sQuery(id+"F0.wireOp",EDGE,"E2"),sQuery(id+"F0.wireOp",EDGE,"E3"),sQuery(id+"F0.wireOp",EDGE,"E4"),sQuery(id+"F0.wireOp",EDGE,"E5"),sQuery(id+"F0.wireOp",EDGE,"E6"),sQuery(id+"F0.wireOp",EDGE,"E7"),sQuery(id+"F0.wireOp",EDGE,"E8"),sQuery(id+"F0.wireOp",EDGE,"E9"),sQuery(id+"F0.wireOp",EDGE,"E10"),sQuery(id+"F0.wireOp",EDGE,"E11"),sQuery(id+"F0.wireOp",EDGE,"E12"),sQuery(id+"F0.wireOp",EDGE,"E13"),sQuery(id+"F0.wireOp",EDGE,"E14"),sQuery(id+"F0.wireOp",EDGE,"E15"),sQuery(id+"F0.wireOp",EDGE,"E16"),sQuery(id+"F0.wireOp",EDGE,"E17"),sQuery(id+"F0.wireOp",EDGE,"E18"),sQuery(id+"F0.wireOp",EDGE,"E19"),sQuery(id+"F0.wireOp",EDGE,"E20"),sQuery(id+"F0.wireOp",EDGE,"E21"),sQuery(id+"F0.wireOp",EDGE,"E22"),sQuery(id+"F0.wireOp",EDGE,"E23"),sQuery(id+"F0.wireOp",EDGE,"E24")])]});
            var Q1;
            Q1=qCreatedBy(makeId("Origin.pointOp"),VERTEX);
            transform(context, id + "F18", {"entities" : qUnion([Q0]), "transformType" : TransformType.SCALE_UNIFORMLY, "scale" : .5, "scalePoint" : qUnion([Q1]), "makeCopy" : false});
        }
        {
            var Q0;
            Q0=makeQuery(id+"F1.opExtrude","SWEPT_BODY",BODY,{"disambiguationData":[OSD([sQuery(id+"F0.wireOp",EDGE,"E0"),sQuery(id+"F0.wireOp",EDGE,"E1"),sQuery(id+"F0.wireOp",EDGE,"E2"),sQuery(id+"F0.wireOp",EDGE,"E3"),sQuery(id+"F0.wireOp",EDGE,"E4"),sQuery(id+"F0.wireOp",EDGE,"E5"),sQuery(id+"F0.wireOp",EDGE,"E6"),sQuery(id+"F0.wireOp",EDGE,"E7"),sQuery(id+"F0.wireOp",EDGE,"E8"),sQuery(id+"F0.wireOp",EDGE,"E9"),sQuery(id+"F0.wireOp",EDGE,"E10"),sQuery(id+"F0.wireOp",EDGE,"E11"),sQuery(id+"F0.wireOp",EDGE,"E12"),sQuery(id+"F0.wireOp",EDGE,"E13"),sQuery(id+"F0.wireOp",EDGE,"E14"),sQuery(id+"F0.wireOp",EDGE,"E15"),sQuery(id+"F0.wireOp",EDGE,"E16"),sQuery(id+"F0.wireOp",EDGE,"E17"),sQuery(id+"F0.wireOp",EDGE,"E18"),sQuery(id+"F0.wireOp",EDGE,"E19"),sQuery(id+"F0.wireOp",EDGE,"E20"),sQuery(id+"F0.wireOp",EDGE,"E21"),sQuery(id+"F0.wireOp",EDGE,"E22"),sQuery(id+"F0.wireOp",EDGE,"E23"),sQuery(id+"F0.wireOp",EDGE,"E24")])]});
            var Q1;
            Q1=qCreatedBy(makeId("Origin.pointOp"),VERTEX);
            transform(context, id + "F19", {"entities" : qUnion([Q0]), "transformType" : TransformType.SCALE_UNIFORMLY, "scale" : .25, "scalePoint" : qUnion([Q1]), "makeCopy" : false});
        }
        {
            var Q0;
            Q0=makeQuery(id+"F1.opExtrude","SWEPT_BODY",BODY,{"disambiguationData":[OSD([sQuery(id+"F0.wireOp",EDGE,"E0"),sQuery(id+"F0.wireOp",EDGE,"E1"),sQuery(id+"F0.wireOp",EDGE,"E2"),sQuery(id+"F0.wireOp",EDGE,"E3"),sQuery(id+"F0.wireOp",EDGE,"E4"),sQuery(id+"F0.wireOp",EDGE,"E5"),sQuery(id+"F0.wireOp",EDGE,"E6"),sQuery(id+"F0.wireOp",EDGE,"E7"),sQuery(id+"F0.wireOp",EDGE,"E8"),sQuery(id+"F0.wireOp",EDGE,"E9"),sQuery(id+"F0.wireOp",EDGE,"E10"),sQuery(id+"F0.wireOp",EDGE,"E11"),sQuery(id+"F0.wireOp",EDGE,"E12"),sQuery(id+"F0.wireOp",EDGE,"E13"),sQuery(id+"F0.wireOp",EDGE,"E14"),sQuery(id+"F0.wireOp",EDGE,"E15"),sQuery(id+"F0.wireOp",EDGE,"E16"),sQuery(id+"F0.wireOp",EDGE,"E17"),sQuery(id+"F0.wireOp",EDGE,"E18"),sQuery(id+"F0.wireOp",EDGE,"E19"),sQuery(id+"F0.wireOp",EDGE,"E20"),sQuery(id+"F0.wireOp",EDGE,"E21"),sQuery(id+"F0.wireOp",EDGE,"E22"),sQuery(id+"F0.wireOp",EDGE,"E23"),sQuery(id+"F0.wireOp",EDGE,"E24")])]});
            var Q1;
            Q1=qCreatedBy(makeId("Origin.pointOp"),VERTEX);
            transform(context, id + "F20", {"entities" : qUnion([Q0]), "transformType" : TransformType.SCALE_UNIFORMLY, "scale" : .5, "scalePoint" : qUnion([Q1]), "makeCopy" : false});
        }
    });
